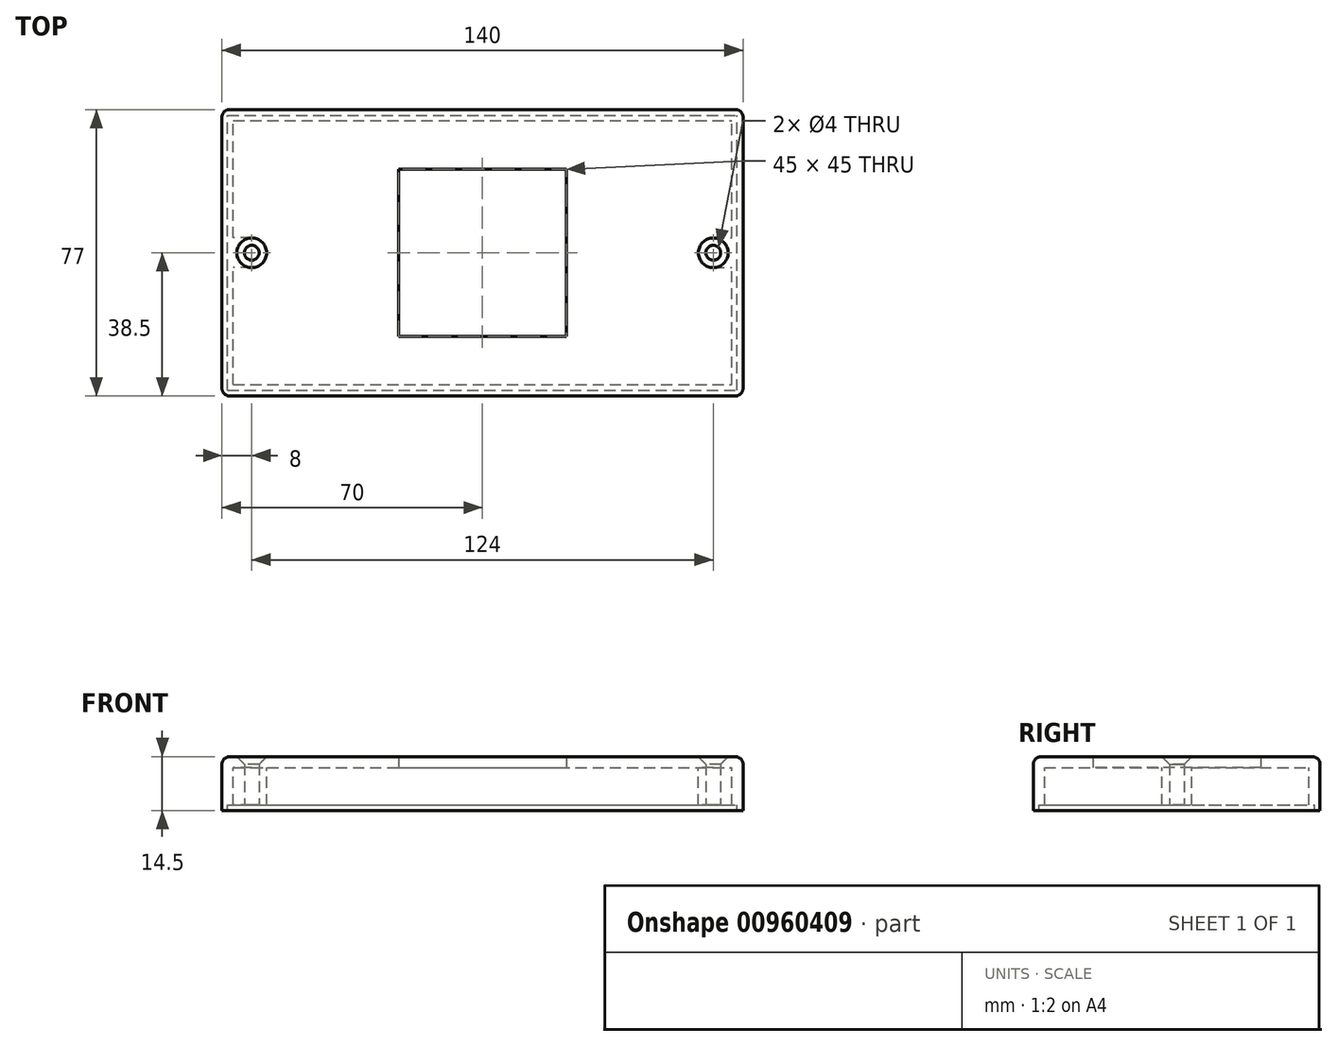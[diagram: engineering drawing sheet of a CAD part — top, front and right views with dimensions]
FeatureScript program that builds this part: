
annotation { "Feature Type Name" : "Feature", "Feature Type Description" : "" }
export const myFeature = defineFeature(function(context is Context, id is Id, definition is map)
    precondition{}
    {
        {
            var Q0;
            Q0=qCreatedBy(makeId("Top.planeOp"),FACE);
            var sketch = newSketch(context, id + "F0", { "sketchPlane" : qUnion([Q0])});
            skLineSegment(sketch, "E0.bottom", {"start": v(-70, 38.5) * mm, "end": v(70, 38.5) * mm});
            skLineSegment(sketch, "E0.top", {"start": v(-70, -38.5) * mm, "end": v(70, -38.5) * mm});
            skLineSegment(sketch, "E0.left", {"start": v(-70, 38.5) * mm, "end": v(-70, -38.5) * mm});
            skLineSegment(sketch, "E0.right", {"start": v(70, 38.5) * mm, "end": v(70, -38.5) * mm});
            skLineSegment(sketch, "E1.bottom", {"start": v(-22.5, 22.5) * mm, "end": v(22.5, 22.5) * mm});
            skLineSegment(sketch, "E1.top", {"start": v(-22.5, -22.5) * mm, "end": v(22.5, -22.5) * mm});
            skLineSegment(sketch, "E1.left", {"start": v(-22.5, 22.5) * mm, "end": v(-22.5, -22.5) * mm});
            skLineSegment(sketch, "E1.right", {"start": v(22.5, 22.5) * mm, "end": v(22.5, -22.5) * mm});
            skCircle(sketch, "E2", {"center": v(-62, 0) * mm, "radius": 2 * mm});
            skCircle(sketch, "E3", {"center": v(-62, 0) * mm, "radius": 4 * mm});
            skCircle(sketch, "E4", {"center": v(62, 0) * mm, "radius": 2 * mm});
            skCircle(sketch, "E5", {"center": v(62, 0) * mm, "radius": 4 * mm});
            skSolve(sketch);
        }
        {
            var Q0;
            Q0 = qSketchRegion(id + "F0", true);
            var Q1;
            Q1=makeQuery(id+"F0.imprint","IMPRINT",FACE,{"disambiguationData":[TD([[makeQuery(id+"F0.imprint","IMPRINT",EDGE,{"derivedFrom":sQuery(id+"F0.wireOp",EDGE,"E2")}),-1.0]])]});
            var Q2;
            Q2=makeQuery(id+"F0.imprint","IMPRINT",FACE,{"disambiguationData":[TD([[makeQuery(id+"F0.imprint","IMPRINT",EDGE,{"derivedFrom":sQuery(id+"F0.wireOp",EDGE,"E4")}),-1.0]])]});
            extrude(context, id + "F1", {"entities" : qUnion([Q0, Q1, Q2]), "depth" : 3 * mm, "offsetDistance" : 25 * mm});
        }
        {
            var Q0;
            Q0=makeQuery(id+"F1.opExtrude","CAP_FACE",FACE,{"disambiguationData":[OSD([sQuery(id+"F0.wireOp",EDGE,"E0.bottom"),sQuery(id+"F0.wireOp",EDGE,"E0.top"),sQuery(id+"F0.wireOp",EDGE,"E0.left"),sQuery(id+"F0.wireOp",EDGE,"E0.right"),sQuery(id+"F0.wireOp",EDGE,"E1.bottom"),sQuery(id+"F0.wireOp",EDGE,"E1.top"),sQuery(id+"F0.wireOp",EDGE,"E1.left"),sQuery(id+"F0.wireOp",EDGE,"E1.right")])],"isStart":true});
            var sketch = newSketch(context, id + "F2", { "sketchPlane" : qUnion([Q0])});
            skLineSegment(sketch, "E6.bottom", {"start": v(-70, 38.5) * mm, "end": v(70, 38.5) * mm});
            skLineSegment(sketch, "E6.top", {"start": v(-70, -38.5) * mm, "end": v(70, -38.5) * mm});
            skLineSegment(sketch, "E6.left", {"start": v(-70, 38.5) * mm, "end": v(-70, -38.5) * mm});
            skLineSegment(sketch, "E6.right", {"start": v(70, 38.5) * mm, "end": v(70, -38.5) * mm});
            skLineSegment(sketch, "E7.bottom", {"start": v(-67, 35.5) * mm, "end": v(67, 35.5) * mm});
            skLineSegment(sketch, "E7.top", {"start": v(-67, -35.5) * mm, "end": v(67, -35.5) * mm});
            skLineSegment(sketch, "E7.left", {"start": v(-67, 35.5) * mm, "end": v(-67, -35.5) * mm});
            skLineSegment(sketch, "E7.right", {"start": v(67, 35.5) * mm, "end": v(67, -35.5) * mm});
            skCircle(sketch, "E8", {"center": v(-62, 0) * mm, "radius": 4 * mm});
            skCircle(sketch, "E9", {"center": v(62, 0) * mm, "radius": 4 * mm});
            skCircle(sketch, "E10", {"center": v(-62, 0) * mm, "radius": 2 * mm});
            skCircle(sketch, "E11", {"center": v(62, 0) * mm, "radius": 2 * mm});
            skLineSegment(sketch, "E12", {"start": v(62, 4) * mm, "end": v(67, 4) * mm});
            skLineSegment(sketch, "E13", {"start": v(62, -4) * mm, "end": v(67, -4) * mm});
            skLineSegment(sketch, "E14", {"start": v(-62, 4) * mm, "end": v(-67, 4) * mm});
            skLineSegment(sketch, "E15", {"start": v(-62, -4) * mm, "end": v(-67, -4) * mm});
            skSolve(sketch);
        }
        {
            var Q0;
            Q0 = qSketchRegion(id + "F2", true);
            var Q1;
            Q1=makeQuery(id+"F2.imprint","IMPRINT",FACE,{"disambiguationData":[TD([[makeQuery(id+"F2.imprint","IMPRINT",EDGE,{"derivedFrom":sQuery(id+"F2.wireOp",EDGE,"E8")}),1.0]])]});
            var Q2;
            Q2=makeQuery(id+"F2.imprint","IMPRINT",FACE,{"disambiguationData":[TD([[makeQuery(id+"F2.imprint","IMPRINT",EDGE,{"derivedFrom":sQuery(id+"F2.wireOp",EDGE,"E9")}),1.0]])]});
            var Q3;
            {var subQ0=sQuery(id+"F2.wireOp",EDGE,"E14");Q3=makeQuery(id+"F2.imprint","IMPRINT",FACE,{"disambiguationData":[TD([[makeQuery(id+"F2.imprint","IMPRINT",EDGE,{"derivedFrom":subQ0}),1.0]])]});}
            var Q4;
            {var subQ0=sQuery(id+"F2.wireOp",EDGE,"E12");Q4=makeQuery(id+"F2.imprint","IMPRINT",FACE,{"disambiguationData":[TD([[makeQuery(id+"F2.imprint","IMPRINT",EDGE,{"derivedFrom":subQ0}),-1.0]])]});}
            extrude(context, id + "F3", {"entities" : qUnion([Q0, Q1, Q2, Q3, Q4]), "operationType" : NewBodyOperationType.ADD, "depth" : 10 * mm, "offsetDistance" : 25 * mm});
        }
        {
            var Q0;
            Q0=makeQuery(id+"F3.opExtrude","CAP_FACE",FACE,{"disambiguationData":[OSD([sQuery(id+"F2.wireOp",EDGE,"E6.bottom"),sQuery(id+"F2.wireOp",EDGE,"E6.top"),sQuery(id+"F2.wireOp",EDGE,"E6.left"),sQuery(id+"F2.wireOp",EDGE,"E6.right"),sQuery(id+"F2.wireOp",EDGE,"E7.bottom"),sQuery(id+"F2.wireOp",EDGE,"E7.top"),sQuery(id+"F2.wireOp",EDGE,"E7.left"),sQuery(id+"F2.wireOp",EDGE,"E7.right")])],"isStart":false});
            var sketch = newSketch(context, id + "F4", { "sketchPlane" : qUnion([Q0])});
            skLineSegment(sketch, "E16.bottom", {"start": v(-70, 38.5) * mm, "end": v(70, 38.5) * mm});
            skLineSegment(sketch, "E16.top", {"start": v(-70, -38.5) * mm, "end": v(70, -38.5) * mm});
            skLineSegment(sketch, "E16.left", {"start": v(-70, 38.5) * mm, "end": v(-70, -38.5) * mm});
            skLineSegment(sketch, "E16.right", {"start": v(70, 38.5) * mm, "end": v(70, -38.5) * mm});
            skLineSegment(sketch, "E17.bottom", {"start": v(-68.5, 37) * mm, "end": v(68.34, 37) * mm});
            skLineSegment(sketch, "E17.top", {"start": v(-68.5, -37) * mm, "end": v(68.34, -37) * mm});
            skLineSegment(sketch, "E17.left", {"start": v(-68.5, 37) * mm, "end": v(-68.5, -37) * mm});
            skLineSegment(sketch, "E17.right", {"start": v(68.34, 37) * mm, "end": v(68.34, -37) * mm});
            skSolve(sketch);
        }
        {
            var Q0;
            Q0 = qSketchRegion(id + "F4", true);
            extrude(context, id + "F5", {"entities" : qUnion([Q0]), "operationType" : NewBodyOperationType.ADD, "depth" : 1.5 * mm, "offsetDistance" : 25 * mm});
        }
        {
            var Q0;
            Q0=makeQuery(id+"F1.opExtrude","CAP_EDGE",EDGE,{"disambiguationData":[OSD([sQuery(id+"F0.wireOp",EDGE,"E0.top")])],"isStart":false});
            var Q1;
            Q1=makeQuery(id+"F1.opExtrude","CAP_EDGE",EDGE,{"disambiguationData":[OSD([sQuery(id+"F0.wireOp",EDGE,"E0.right")])],"isStart":false});
            var Q2;
            Q2=makeQuery(id+"F1.opExtrude","CAP_EDGE",EDGE,{"disambiguationData":[OSD([sQuery(id+"F0.wireOp",EDGE,"E0.bottom")])],"isStart":false});
            var Q3;
            Q3=makeQuery(id+"F1.opExtrude","CAP_EDGE",EDGE,{"disambiguationData":[OSD([sQuery(id+"F0.wireOp",EDGE,"E0.left")])],"isStart":false});
            var Q4;
            Q4=makeQuery(id+"F5.boolean.opBoolean","MERGE",EDGE,{"derivedFrom":[makeQuery(id+"F3.boolean.opBoolean","MERGE",EDGE,{"derivedFrom":[makeQuery(id+"F1.opExtrude","SWEPT_EDGE",EDGE,{"disambiguationData":[OSD([sQuery(id+"F0.wireOp",EDGE,"E0.bottom"),sQuery(id+"F0.wireOp",EDGE,"E0.left")])]}),makeQuery(id+"F3.opExtrude","SWEPT_EDGE",EDGE,{"disambiguationData":[OSD([sQuery(id+"F2.wireOp",EDGE,"E6.top"),sQuery(id+"F2.wireOp",EDGE,"E6.left")])]})]}),makeQuery(id+"F5.opExtrude","SWEPT_EDGE",EDGE,{"disambiguationData":[OSD([sQuery(id+"F4.wireOp",EDGE,"E16.top"),sQuery(id+"F4.wireOp",EDGE,"E16.left")])]})]});
            var Q5;
            Q5=makeQuery(id+"F5.boolean.opBoolean","MERGE",EDGE,{"derivedFrom":[makeQuery(id+"F3.boolean.opBoolean","MERGE",EDGE,{"derivedFrom":[makeQuery(id+"F1.opExtrude","SWEPT_EDGE",EDGE,{"disambiguationData":[OSD([sQuery(id+"F0.wireOp",EDGE,"E0.top"),sQuery(id+"F0.wireOp",EDGE,"E0.left")])]}),makeQuery(id+"F3.opExtrude","SWEPT_EDGE",EDGE,{"disambiguationData":[OSD([sQuery(id+"F2.wireOp",EDGE,"E6.bottom"),sQuery(id+"F2.wireOp",EDGE,"E6.left")])]})]}),makeQuery(id+"F5.opExtrude","SWEPT_EDGE",EDGE,{"disambiguationData":[OSD([sQuery(id+"F4.wireOp",EDGE,"E16.bottom"),sQuery(id+"F4.wireOp",EDGE,"E16.left")])]})]});
            var Q6;
            Q6=makeQuery(id+"F5.boolean.opBoolean","MERGE",EDGE,{"derivedFrom":[makeQuery(id+"F3.boolean.opBoolean","MERGE",EDGE,{"derivedFrom":[makeQuery(id+"F1.opExtrude","SWEPT_EDGE",EDGE,{"disambiguationData":[OSD([sQuery(id+"F0.wireOp",EDGE,"E0.top"),sQuery(id+"F0.wireOp",EDGE,"E0.right")])]}),makeQuery(id+"F3.opExtrude","SWEPT_EDGE",EDGE,{"disambiguationData":[OSD([sQuery(id+"F2.wireOp",EDGE,"E6.bottom"),sQuery(id+"F2.wireOp",EDGE,"E6.right")])]})]}),makeQuery(id+"F5.opExtrude","SWEPT_EDGE",EDGE,{"disambiguationData":[OSD([sQuery(id+"F4.wireOp",EDGE,"E16.bottom"),sQuery(id+"F4.wireOp",EDGE,"E16.right")])]})]});
            var Q7;
            Q7=makeQuery(id+"F5.boolean.opBoolean","MERGE",EDGE,{"derivedFrom":[makeQuery(id+"F3.boolean.opBoolean","MERGE",EDGE,{"derivedFrom":[makeQuery(id+"F1.opExtrude","SWEPT_EDGE",EDGE,{"disambiguationData":[OSD([sQuery(id+"F0.wireOp",EDGE,"E0.bottom"),sQuery(id+"F0.wireOp",EDGE,"E0.right")])]}),makeQuery(id+"F3.opExtrude","SWEPT_EDGE",EDGE,{"disambiguationData":[OSD([sQuery(id+"F2.wireOp",EDGE,"E6.top"),sQuery(id+"F2.wireOp",EDGE,"E6.right")])]})]}),makeQuery(id+"F5.opExtrude","SWEPT_EDGE",EDGE,{"disambiguationData":[OSD([sQuery(id+"F4.wireOp",EDGE,"E16.top"),sQuery(id+"F4.wireOp",EDGE,"E16.right")])]})]});
            fillet(context, id + "F6", {"entities" : qUnion([Q0, Q1, Q2, Q3, Q4, Q5, Q6, Q7]), "radius" : 2 * mm, "tangentPropagation" : true, "allowEdgeOverflow" : false});
        }
        {
            var Q0;
            Q0=makeQuery(id+"F1.opExtrude","CAP_EDGE",EDGE,{"disambiguationData":[OSD([sQuery(id+"F0.wireOp",EDGE,"E2")])],"isStart":false});
            var Q1;
            Q1=makeQuery(id+"F1.opExtrude","CAP_EDGE",EDGE,{"disambiguationData":[OSD([sQuery(id+"F0.wireOp",EDGE,"E4")])],"isStart":false});
            chamfer(context, id + "F7", {"entities" : qUnion([Q0, Q1]), "width" : 2 * mm, "tangentPropagation" : true});
        }
    });
